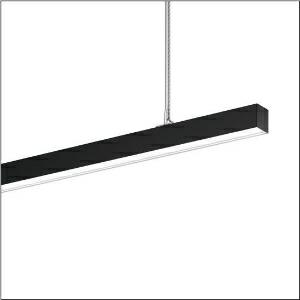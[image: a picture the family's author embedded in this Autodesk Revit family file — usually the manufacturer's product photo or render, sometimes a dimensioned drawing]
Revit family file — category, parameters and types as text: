
# Revit family: silica_r__21_51mx33tat7b_231b
name_source: partatom
category: Lighting Fixtures
units: mm (PartAtom-declared; Revit-internal decimal feet)

## family parameters
Cut with Voids When Loaded = No
Host = Face
Light Source = No
Part Type = Normal
Room Calculation Point = No
Round Connector Dimension = Use Diameter
Shared = No

## types (1)
- --- (1 x LED, 5740 lm, 53.8 W, 6500K)
    Apparent Load = 54 VA
    CIE Flux Codes = 78 96 99 56 100
    Color Rendering = 80
    Color Temperature = 6500K
    Default Elevation = 1800 mm
    Description = Silica® 21, office luminaire, primary optical cover: prismatic diffuser, of PMMA, CAT 2 (L<= 3000cd/m²), light emission: direct/indirect distribution, primary light characteristic: symmetric, installation type: suspended mounting, LED, rated luminous flux: 5.740lm, luminous efficacy: 102lm/W, light colour: 8tw, colour temperature: 2700..6500K, control gear: ECG DALI, with terminal, 3+2-pole, max. 2.5mm², mains connection: 220..240V, AC, 50/60Hz, rated input power: 56.5W, luminaire housing, of aluminium, jet black (RAL 9005), length: 1.204mm, width: 53mm, height: 53mm, protection rating (complete): IP20, insulation class (complete): insulation class I (protective earthing), certification: CE, permissible operating ambient temperature: 0..+35°C, standard: EN 50419, packaging unit: 1 piece
    Height = 53 mm
    Lamp = 1 x LED
    Lamp Light Flux = 5740 lm
    Lamp Power = 53.8 W
    Lamp count = 1
    Length = 1204 mm
    Luminous efficacy = 107 lm/W
    Manufacturer = Siteco
    ModVariant = No
    Model = 51MX33TAT7B
    Mounting Place = Ceiling
    Mounting Type = Pendant
    Number of Poles = 1
    OnlyDefault = Yes
    Power Factor = 1
    Product Name = Silica® 21
    Product group = office luminaire | ceiling pendant
    ProductGroupID = 905
    Protection Class = Protection class I
    Protection Degree = IP 20
    RLX_Detail_Level = 1
    RlxData = <blob elided: 22925 chars, md5=4e368d35>
    Socket = socket
    Standby Power = 0 W
    System Light Flux = 5740 lm
    System Power = 54 W
    Type Comments = individual setting
    Type Image = l_1251735.jpg
    URL = http://relux.com
    VarID = @adj_045855
    Voltage = 0 V
    Weight = 0.00 kg
    Width = 53 mm

## geometry (parser evidence)
native form markers: Blend x4, Sweep x11
no freeform markers — native parametric forms only
